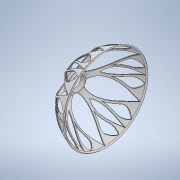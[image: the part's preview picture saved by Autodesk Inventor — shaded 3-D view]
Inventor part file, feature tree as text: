
AUTODESK INVENTOR PART (.ipt)
format: ipt  version: 2020 (Build 240168000, 168)  size: 3,204,608 bytes
history: native  units: mm
features: fillet x7, pattern_circular x4, sketch x2, revolve x1, extrude x1
ambient origin geometry x8: Origin, YZ Plane, XZ Plane, XY Plane, X Axis, Y Axis, Z Axis, Center Point
bodies: Solid1 (feature_tree)
feature tree (15):
  revolve  "Revolution1"  [1 undecoded]
  sketch  "Sketch2"  dims[d7=65.0mm d8=1.0mm d10=0.0mm d11=0.0mm d14=90.0deg d15=3.0mm d23=0.0mm d24=0.0mm d27=30.0mm d28=30.0mm d44=3.0mm d45=5.0mm d47=0.0mm d49=50.0mm d53=45.0deg d56=2.0mm d57=65.0mm d62=25.0mm d63=128.0mm d67=0.0mm d68=60.0deg d69=25.0mm d70=0.0mm d71=3.0mm d72=3.0mm d94=30.0deg d95=25.0mm d96=25.0mm d97=0.0mm d98=3.0mm d99=3.0mm d100=50.0mm d101=0.0mm d105=115.555556mm d106=15.0mm d107=5.0mm d108=5.0mm d109=15.0mm d110=2.0mm d111=60.0mm d112=360.0deg d114=2.0mm d115=0.5mm d116=0.5mm d117=0.5mm d118=0.5mm d119=60.0mm d120=360.0deg d122=60.0mm d123=360.0deg d125=60.0mm d126=360.0deg d25=0.5mm d26=0.872665mm d87=0.5mm d88=0.872665mm d89=0.5mm d90=0.872665mm]
  fillet  "Fillet2"  [1 undecoded]
  extrude  "Extrusion5"  Depth=1.0mm
  fillet  "Fillet3"  [1 undecoded]
  pattern_circular  "Circular Pattern5"  [2 undecoded]
  fillet  "Fillet4"  [1 undecoded]
  fillet  "Fillet5"  Radius=3.0mm
  fillet  "Fillet6"  [1 undecoded]
  fillet  "Fillet7"  [1 undecoded]
  fillet  "Fillet8"  Radius=30.0mm
  pattern_circular  "Circular Pattern6"  Count=3  [1 undecoded]
  pattern_circular  "Circular Pattern7"  [2 undecoded]
  pattern_circular  "Circular Pattern8"  [2 undecoded]
  sketch  "Sketch1"  dims[d0=11.0mm d1=7.0mm d4=90.0deg]
note: 13 required parameter values undecoded (feature->parameter linkage not recoverable at this tier; creation-order binding heuristic only, values carry confidence <= 0.55)